# Revit family: IS_Idealrain_Multiproduct_BIM_GB_B9442;B9443
name_source: partatom
category: Plumbing Fixtures
revit_build: Autodesk Revit MEP 2014 (Build: 20130308_1515(x64)
units: mm (PartAtom-declared; Revit-internal decimal feet)

## types (2) — shared parameters
Accessories = www.idealspec.co.uk
AreaUnits = millimeters
Assembly Code = C1030200
AssetType = Fixed
BREEAMApproved = No
Brand = Ideal Standard
Color = Chrome
ConnectionType = Plumbing
Default Elevation = 2100 mm
DurationUnit = year
ECA = No
ExpectedLife = 30
FaucetFunction = MIXED
FaucetOperation = LEVERHANDLE
Finish = Chrome
Help = www.idealspec.co.uk/contact-us.html
IfcExportAs = IfcValveType
IfcExportType = SHOWERS
InstallationInstructions = www.idealspec.co.uk/resources.html
LinearUnits = millimeters
ManufacturerURL = www.idealspec.co.uk
Material = Brass
MetalMtl = ISI_IdealStandard_Brassware_Chrome_Render
NBSDescription = Shower head
NBSReference = 45-35-70/333
Name = ShowerMixers_IdealRain_A5691AA_IdealStandard
PlasticMtl = ISI_IdealStandard_Brassware_Plastic_Render
Shape = Sculptured
Space = Internal
SpareParts = www.fastpart-spares.co.uk
TMV3 = Yes
TestPressure = 10 Bar
URL = www.idealspec.co.uk
Uniclass2015Code = Pr_40_20_87_76
Uniclass2015Title = Shower head
Uniclass2015Version = Product v1.1
Version = 1
VolumeUnits = Litres
WRAS = Yes
WarrantyDescription = Manufacturers Warranty
WarrantyDurationParts = 5
WarrantyDurationUnit = year
WaterEfficientProduct = No
WorkingPressure = 3 Bar
zero-valued in all types: CWFU, Cost, HWFU, NominalHeight, WFU

## per-type parameters (varying)
| type | 200mm | 300mm | BIMObjectName | BarCode | Description | Features | Model | NettWeight | NominalLength | NominalWidth | ProductInformation | Size |
| B9442AA - Idealrain Round Shower - 200mm | Yes | No | ISI_IdealStandard_ShowerMixers_IdealRain_B9442AA | 3800861023890 | Idealrain round rain shower Ø200mm | round rain shower Ø200mm | B9442AA | 0.96Kg | 200 mm  [stored 0.656168 ft] | 200 mm  [stored 0.656168 ft] | www.idealspec.co.uk/assets/datasheet/B9442AA | 0 x 200 x 200 mm |
| B9443AA - Idealrain Round Shower - 300mm | No | Yes | ISI_IdealStandard_ShowerMixers_IdealRain_B9443AA | 3800861023906 | Idealrain round rain shower Ø300mm | round rain shower Ø300mm | B9443AA | 1.96Kg | 300 mm  [stored 0.984252 ft] | 300 mm  [stored 0.984252 ft] | www.idealspec.co.uk/assets/datasheet/B9443AA | 0 x 300 x 300 mm |

note: [stored X ft] marks values corroborated as IEEE doubles in the binary element streams (Revit-internal decimal feet)

## geometry (parser evidence)
native form markers: Sweep x2
no freeform markers — native parametric forms only
